# Revit family: Metal_Vented_Lockers-Salsbury_Industries-83000_Series-3_Wide_Units
name_source: partatom
category: Specialty Equipment
revit_build: Autodesk Revit 2016 (Build: 20150714_1515(x64)
units: mm (PartAtom-declared; Revit-internal decimal feet)

## family parameters
Always vertical = Yes
Cut with Voids When Loaded = No
OmniClass Number = 23.40.00.00
OmniClass Title = Equipment and Furnishings
Part Type = Normal
Room Calculation Point = No
Round Connector Dimension = Use Diameter
Shared = No
Work Plane-Based = No

## types (6) — shared parameters
Assembly Code = C1030310
Compartment Divider Height = 22.814 "
Door Location D1 = Vented Metal Locker Doors-15 inch with Hasps : Triple Tier Door - 6 foot
Hasp Handle Material = Plastic - Salsbury Finish - Black
Hasp Plate Rivet Material = Steel -Salsbury Finish - Polished Steel
Individual Door Height = 23.189 "
Manufacturer = Salsbury Industries
MasterFormat Number = 10 51 13
MasterFormat Title = Lockers
OmniClass 23 Number = 23.40.00.00
Type Comments = 15" Wide Vented Metal Locker - Triple Tier
URL = www.lockers.com
Unit Height = 72 "
Vent Array Spacing = 1.187 "
Vent Configuration Height = Vents : 6 foot high vents
Version = 2.0 (02/28/18)
Width = 45.04 "

## per-type parameters (varying)
| type | Base Height | Depth | Description | Model | OmniClass 23 Title | Sloping Hood Height | Standard Leg Base | Vent Array 1 | Vent Array 2 | Vent Offset | Zee Base |
| 83365 - with Standard 6" High Legs | 6 " | 15.01 " | 3 Wide - 6 Feet High - 15 Inches Deep | 83365 | Equipment and Furnishings | 8.682 " | Metal Locker Legs - 3 Wide : 6" High - 45"W x 15"D | 8 | 7 | 3.5 " | Metal Locker Zee Base - 3 Wide : None |
| 83368 - with Standard 6" High Legs | 6 " | 18.01 " | 3 Wide - 6 Feet High - 18 Inches Deep | 83368 | Equipment and Furnishings | 10.739 " | Metal Locker Legs - 3 Wide : 6" High - 45"W x 18"D | 10 | 9 | 3.75 " | Metal Locker Zee Base - 3 Wide : None |
| 83365 - with 77575 Zee Base and 77550 Lockers without Legs | 4 " | 15.01 " | 3 Wide - 6 Feet High - 15 Inches Deep with Zee Base and Lockers without Legs | 83365 with 77575 and 77550 | Equipment and Furnishings | 8.682 " | Metal Locker Legs - 3 Wide : No Legs | 8 | 7 | 3.5 " | Metal Locker Zee Base - 3 Wide : 77575 - 45"W x 15"D |
| 83368 - with 77578 Zee Base and 77550 Lockers without Legs | 4 " | 18.01 " | 3 Wide - 6 Feet High - 18 Inches Deep with Zee Base and Lockers without Legs | 83368 with 77578 and 77550 | Equipment aqnd Furnishings | 10.739 " | Metal Locker Legs - 3 Wide : No Legs | 10 | 9 | 3.75 " | Metal Locker Zee Base - 3 Wide : 77578 - 45"W x 18"D |
| 83365 - with 77550 Lockers without Legs | 0 " | 15.01 " | 3 Wide - 6 Feet High - 15 Inches Deep with Lockers without Legs | 83365 with 77550 | Equipment and Furnishings | 8.682 " | Metal Locker Legs - 3 Wide : No Legs | 8 | 7 | 3.5 " | Metal Locker Zee Base - 3 Wide : None |
| 83368 - with 77550 Lockers without Legs | 0 " | 18.01 " | 3 Wide - 6 Feet High - 18 Inches Deep with Lockers without Legs | 83368 with 77550 | Equipment and Furnishings | 10.739 " | Metal Locker Legs - 3 Wide : No Legs | 10 | 9 | 3.75 " | Metal Locker Zee Base - 3 Wide : None |

## geometry (parser evidence)
native form markers: Sweep x62
no freeform markers — native parametric forms only
